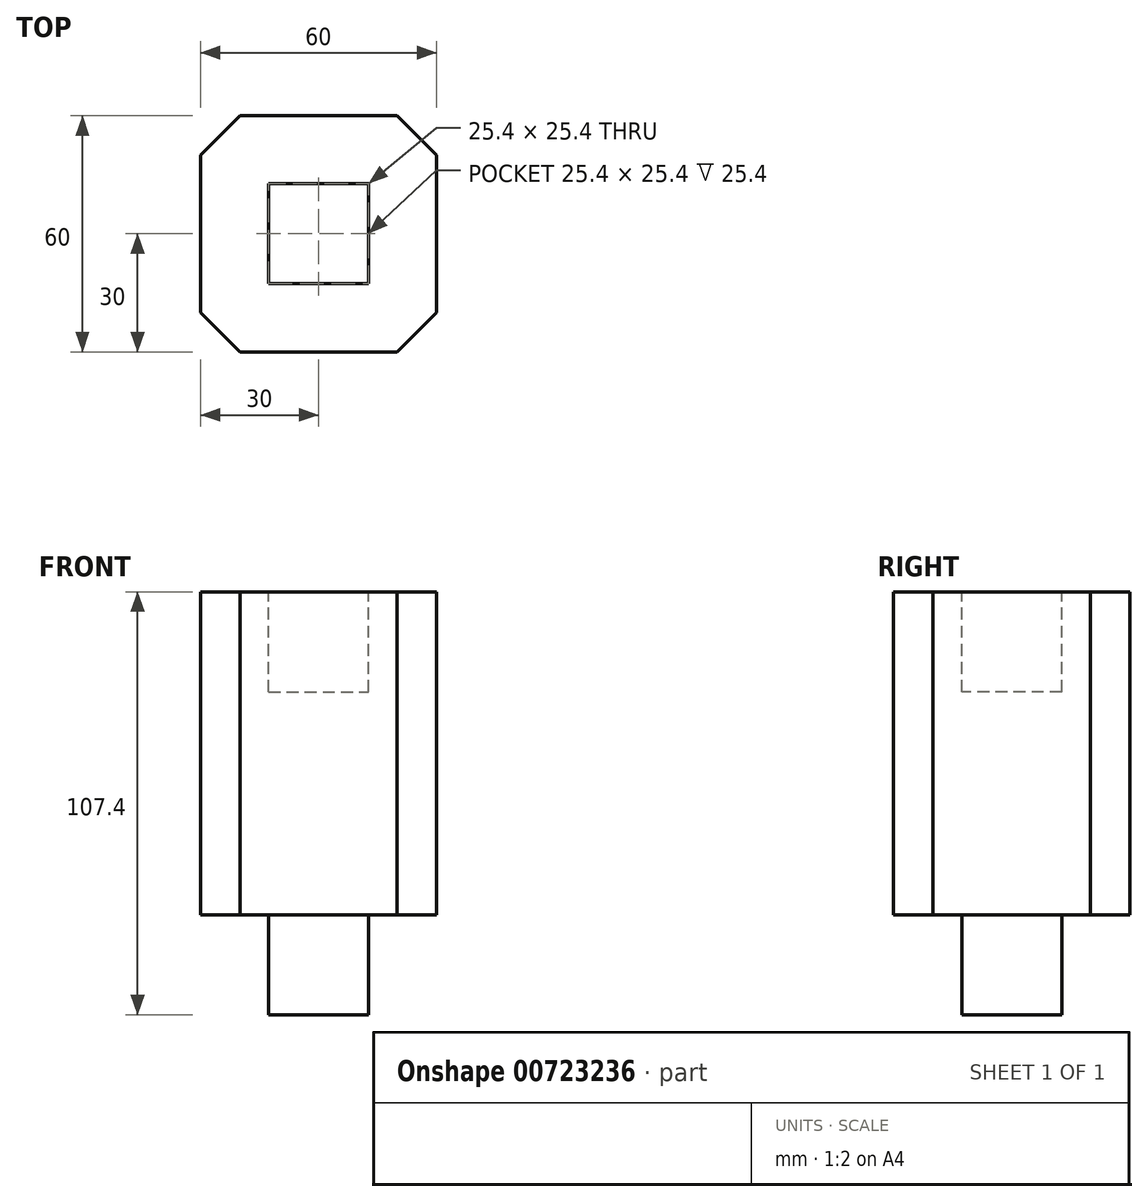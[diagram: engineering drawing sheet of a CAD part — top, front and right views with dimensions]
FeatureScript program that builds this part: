
annotation { "Feature Type Name" : "Feature", "Feature Type Description" : "" }
export const myFeature = defineFeature(function(context is Context, id is Id, definition is map)
    precondition{}
    {
        {
            var Q0;
            Q0=qCreatedBy(makeId("Top.planeOp"),FACE);
            var sketch = newSketch(context, id + "F0", { "sketchPlane" : qUnion([Q0])});
            skLineSegment(sketch, "E0.bottom", {"start": v(-30, 30) * mm, "end": v(30, 30) * mm});
            skLineSegment(sketch, "E0.top", {"start": v(-30, -30) * mm, "end": v(30, -30) * mm});
            skLineSegment(sketch, "E0.left", {"start": v(-30, 30) * mm, "end": v(-30, -30) * mm});
            skLineSegment(sketch, "E0.right", {"start": v(30, 30) * mm, "end": v(30, -30) * mm});
            skSolve(sketch);
        }
        {
            var Q0;
            Q0 = qSketchRegion(id + "F0", true);
            extrude(context, id + "F1", {"entities" : qUnion([Q0]), "depth" : 82 * mm, "offsetDistance" : 25 * mm});
        }
        {
            var Q0;
            Q0=makeQuery(id+"F1.opExtrude","SWEPT_EDGE",EDGE,{"disambiguationData":[OSD([sQuery(id+"F0.wireOp",EDGE,"E0.top"),sQuery(id+"F0.wireOp",EDGE,"E0.right")])]});
            var Q1;
            Q1=makeQuery(id+"F1.opExtrude","SWEPT_EDGE",EDGE,{"disambiguationData":[OSD([sQuery(id+"F0.wireOp",EDGE,"E0.bottom"),sQuery(id+"F0.wireOp",EDGE,"E0.right")])]});
            var Q2;
            Q2=makeQuery(id+"F1.opExtrude","SWEPT_EDGE",EDGE,{"disambiguationData":[OSD([sQuery(id+"F0.wireOp",EDGE,"E0.top"),sQuery(id+"F0.wireOp",EDGE,"E0.left")])]});
            var Q3;
            Q3=makeQuery(id+"F1.opExtrude","SWEPT_EDGE",EDGE,{"disambiguationData":[OSD([sQuery(id+"F0.wireOp",EDGE,"E0.bottom"),sQuery(id+"F0.wireOp",EDGE,"E0.left")])]});
            chamfer(context, id + "F2", {"entities" : qUnion([Q0, Q1, Q2, Q3]), "width" : 10 * mm, "tangentPropagation" : true});
        }
        {
            var Q0;
            Q0=makeQuery(id+"F1.opExtrude","CAP_FACE",FACE,{"disambiguationData":[OSD([sQuery(id+"F0.wireOp",EDGE,"E0.bottom"),sQuery(id+"F0.wireOp",EDGE,"E0.top"),sQuery(id+"F0.wireOp",EDGE,"E0.left"),sQuery(id+"F0.wireOp",EDGE,"E0.right")])],"isStart":false});
            var sketch = newSketch(context, id + "F3", { "sketchPlane" : qUnion([Q0])});
            skLineSegment(sketch, "E1.bottom", {"start": v(-12.7, 12.7) * mm, "end": v(12.7, 12.7) * mm});
            skLineSegment(sketch, "E1.top", {"start": v(-12.7, -12.7) * mm, "end": v(12.7, -12.7) * mm});
            skLineSegment(sketch, "E1.left", {"start": v(-12.7, 12.7) * mm, "end": v(-12.7, -12.7) * mm});
            skLineSegment(sketch, "E1.right", {"start": v(12.7, 12.7) * mm, "end": v(12.7, -12.7) * mm});
            skSolve(sketch);
        }
        {
            var Q0;
            Q0 = qSketchRegion(id + "F3", true);
            extrude(context, id + "F4", {"entities" : qUnion([Q0]), "operationType" : NewBodyOperationType.REMOVE, "oppositeDirection" : true, "depth" : 25.4 * mm, "offsetDistance" : 25 * mm});
        }
        {
            var Q0;
            Q0=makeQuery(id+"F1.opExtrude","CAP_FACE",FACE,{"disambiguationData":[OSD([sQuery(id+"F0.wireOp",EDGE,"E0.bottom"),sQuery(id+"F0.wireOp",EDGE,"E0.top"),sQuery(id+"F0.wireOp",EDGE,"E0.left"),sQuery(id+"F0.wireOp",EDGE,"E0.right")])],"isStart":true});
            var sketch = newSketch(context, id + "F5", { "sketchPlane" : qUnion([Q0])});
            skLineSegment(sketch, "E2.bottom", {"start": v(-12.7, 12.7) * mm, "end": v(12.7, 12.7) * mm});
            skLineSegment(sketch, "E2.top", {"start": v(-12.7, -12.7) * mm, "end": v(12.7, -12.7) * mm});
            skLineSegment(sketch, "E2.left", {"start": v(-12.7, 12.7) * mm, "end": v(-12.7, -12.7) * mm});
            skLineSegment(sketch, "E2.right", {"start": v(12.7, 12.7) * mm, "end": v(12.7, -12.7) * mm});
            skSolve(sketch);
        }
        {
            var Q0;
            Q0 = qSketchRegion(id + "F5", true);
            extrude(context, id + "F6", {"entities" : qUnion([Q0]), "operationType" : NewBodyOperationType.ADD, "depth" : 25.4 * mm, "offsetDistance" : 25 * mm});
        }
    });
